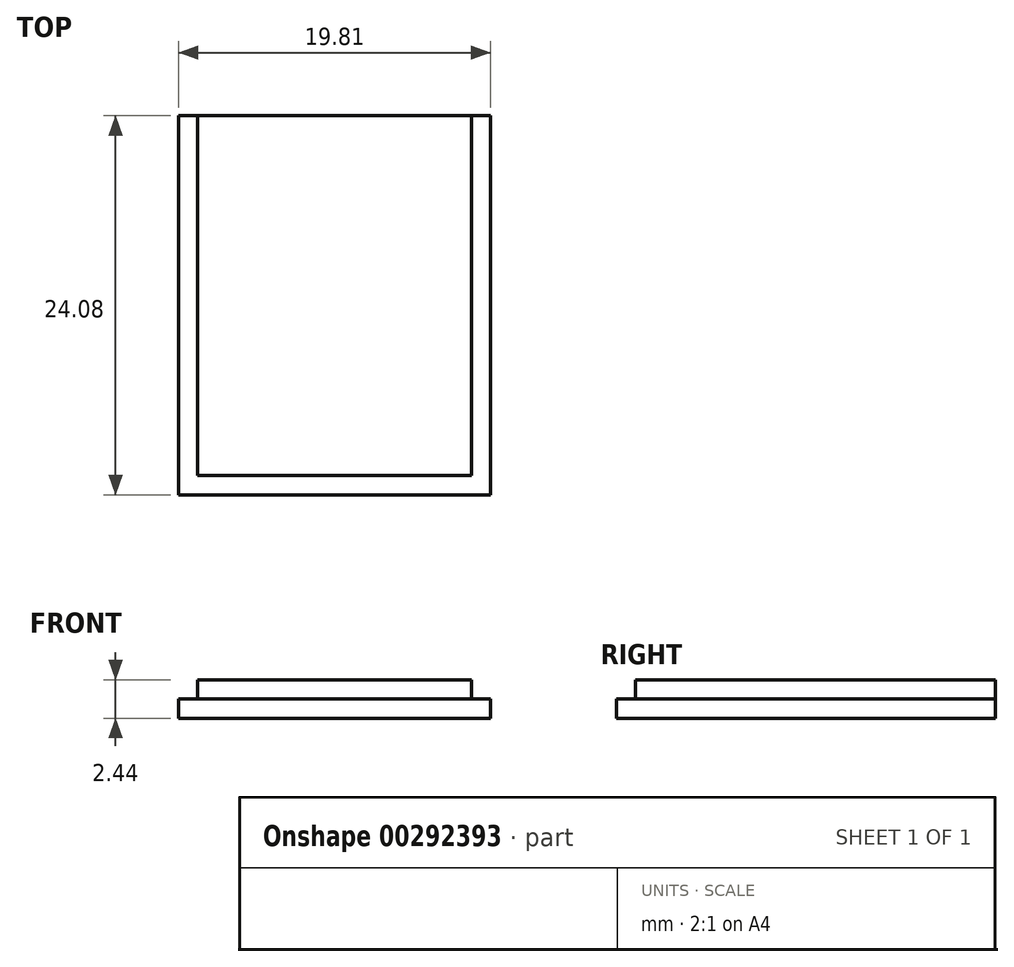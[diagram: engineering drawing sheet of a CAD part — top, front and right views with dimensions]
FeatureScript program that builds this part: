
annotation { "Feature Type Name" : "Feature", "Feature Type Description" : "" }
export const myFeature = defineFeature(function(context is Context, id is Id, definition is map)
    precondition{}
    {
        {
            var Q0;
            Q0=qCreatedBy(makeId("Front.planeOp"),FACE);
            var sketch = newSketch(context, id + "F0", { "sketchPlane" : qUnion([Q0])});
            skLineSegment(sketch, "E0", {"start": v(0, 0) * mm, "end": v(0, 1.22) * mm});
            skLineSegment(sketch, "E1", {"start": v(0, 1.22) * mm, "end": v(1.22, 1.22) * mm});
            skLineSegment(sketch, "E2", {"start": v(1.22, 1.22) * mm, "end": v(1.22, 2.44) * mm});
            skLineSegment(sketch, "E3", {"start": v(1.22, 2.44) * mm, "end": v(18.6, 2.44) * mm});
            skLineSegment(sketch, "E4", {"start": v(18.6, 2.44) * mm, "end": v(18.6, 1.22) * mm});
            skLineSegment(sketch, "E5", {"start": v(18.6, 1.22) * mm, "end": v(19.81, 1.22) * mm});
            skLineSegment(sketch, "E6", {"start": v(19.81, 1.22) * mm, "end": v(19.81, 0) * mm});
            skLineSegment(sketch, "E7", {"start": v(19.81, 0) * mm, "end": v(0, 0) * mm});
            skSolve(sketch);
        }
        {
            var Q0;
            Q0=makeQuery(id+"F0.imprint","IMPRINT",FACE,{"disambiguationData":[TD([[makeQuery(id+"F0.imprint","IMPRINT",EDGE,{"derivedFrom":sQuery(id+"F0.wireOp",EDGE,"E0")}),-1.0]])]});
            extrude(context, id + "F1", {"entities" : qUnion([Q0]), "depth" : 22.86 * mm});
        }
        {
            var Q0;
            Q0=makeQuery(id+"F1.opExtrude","CAP_FACE",FACE,{"disambiguationData":[OSD([sQuery(id+"F0.wireOp",EDGE,"E0"),sQuery(id+"F0.wireOp",EDGE,"E1"),sQuery(id+"F0.wireOp",EDGE,"E2"),sQuery(id+"F0.wireOp",EDGE,"E3"),sQuery(id+"F0.wireOp",EDGE,"E4"),sQuery(id+"F0.wireOp",EDGE,"E5"),sQuery(id+"F0.wireOp",EDGE,"E6"),sQuery(id+"F0.wireOp",EDGE,"E7")])],"isStart":false});
            var sketch = newSketch(context, id + "F2", { "sketchPlane" : qUnion([Q0])});
            skLineSegment(sketch, "E8", {"start": v(0, 0) * mm, "end": v(0, 1.22) * mm});
            skLineSegment(sketch, "E9", {"start": v(0, 1.22) * mm, "end": v(19.81, 1.22) * mm});
            skLineSegment(sketch, "E10", {"start": v(19.81, 1.22) * mm, "end": v(19.81, 0) * mm});
            skLineSegment(sketch, "E11", {"start": v(19.81, 0) * mm, "end": v(0, 0) * mm});
            skSolve(sketch);
        }
        {
            var Q0;
            {var subQ3=sQuery(id+"F2.wireOp",EDGE,"E8");Q0=makeQuery(id+"F2.imprint","IMPRINT",FACE,{"disambiguationData":[TD([[makeQuery(id+"F2.imprint","IMPRINT",EDGE,{"derivedFrom":subQ3}),-1.0]])]});}
            extrude(context, id + "F3", {"entities" : qUnion([Q0]), "operationType" : NewBodyOperationType.ADD, "depth" : 1.22 * mm});
        }
    });
